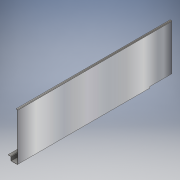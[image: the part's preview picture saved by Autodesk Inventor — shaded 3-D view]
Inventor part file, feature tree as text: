
AUTODESK INVENTOR PART (.ipt)
format: ipt  version: 2017 (Build 210142000, 142)  size: 220,160 bytes
history: native  units: in
note: dims shown in document units (in); Inventor stores cm internally (conversion verified against a paired STEP export)
features: other x5, sketch x3, plane x1
ambient origin geometry x8: Origin, YZ Plane, XZ Plane, XY Plane, X Axis, Y Axis, Z Axis, Center Point
bodies: Solid1 (feature_tree)
feature tree (9):
  other  "Lateral -A.ipt"
  plane  "Work Plane1"
  other  "Decal1"
  other  "Solid1::Lateral -A.ipt"
  other  "TaggingFeature1"
  sketch  "Sketch1"  dims[d0=0.3937in]
  sketch  "Sketch2"  dims[d1=7.874in]
  sketch  "Sketch3"
  other  "Image1"
